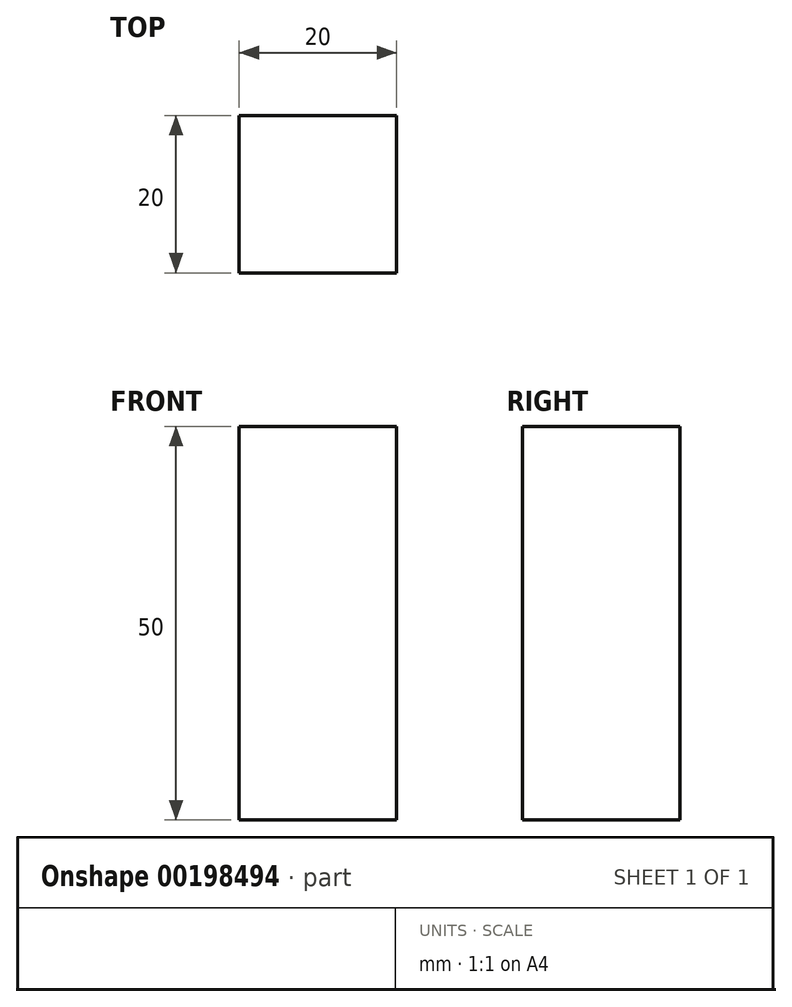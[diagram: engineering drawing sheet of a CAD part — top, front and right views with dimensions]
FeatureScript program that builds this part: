
annotation { "Feature Type Name" : "Feature", "Feature Type Description" : "" }
export const myFeature = defineFeature(function(context is Context, id is Id, definition is map)
    precondition{}
    {
        {
            var Q0;
            Q0=qCreatedBy(makeId("Top.planeOp"),FACE);
            var sketch = newSketch(context, id + "F0", { "sketchPlane" : qUnion([Q0])});
            skLineSegment(sketch, "E0.bottom", {"start": v(0, 0) * mm, "end": v(20, 0) * mm});
            skLineSegment(sketch, "E0.top", {"start": v(0, -20) * mm, "end": v(20, -20) * mm});
            skLineSegment(sketch, "E0.left", {"start": v(0, 0) * mm, "end": v(0, -20) * mm});
            skLineSegment(sketch, "E0.right", {"start": v(20, 0) * mm, "end": v(20, -20) * mm});
            skSolve(sketch);
        }
        {
            var Q0;
            Q0 = qSketchRegion(id + "F0", true);
            extrude(context, id + "F1", {"entities" : qUnion([Q0]), "depth" : 50 * mm});
        }
    });
